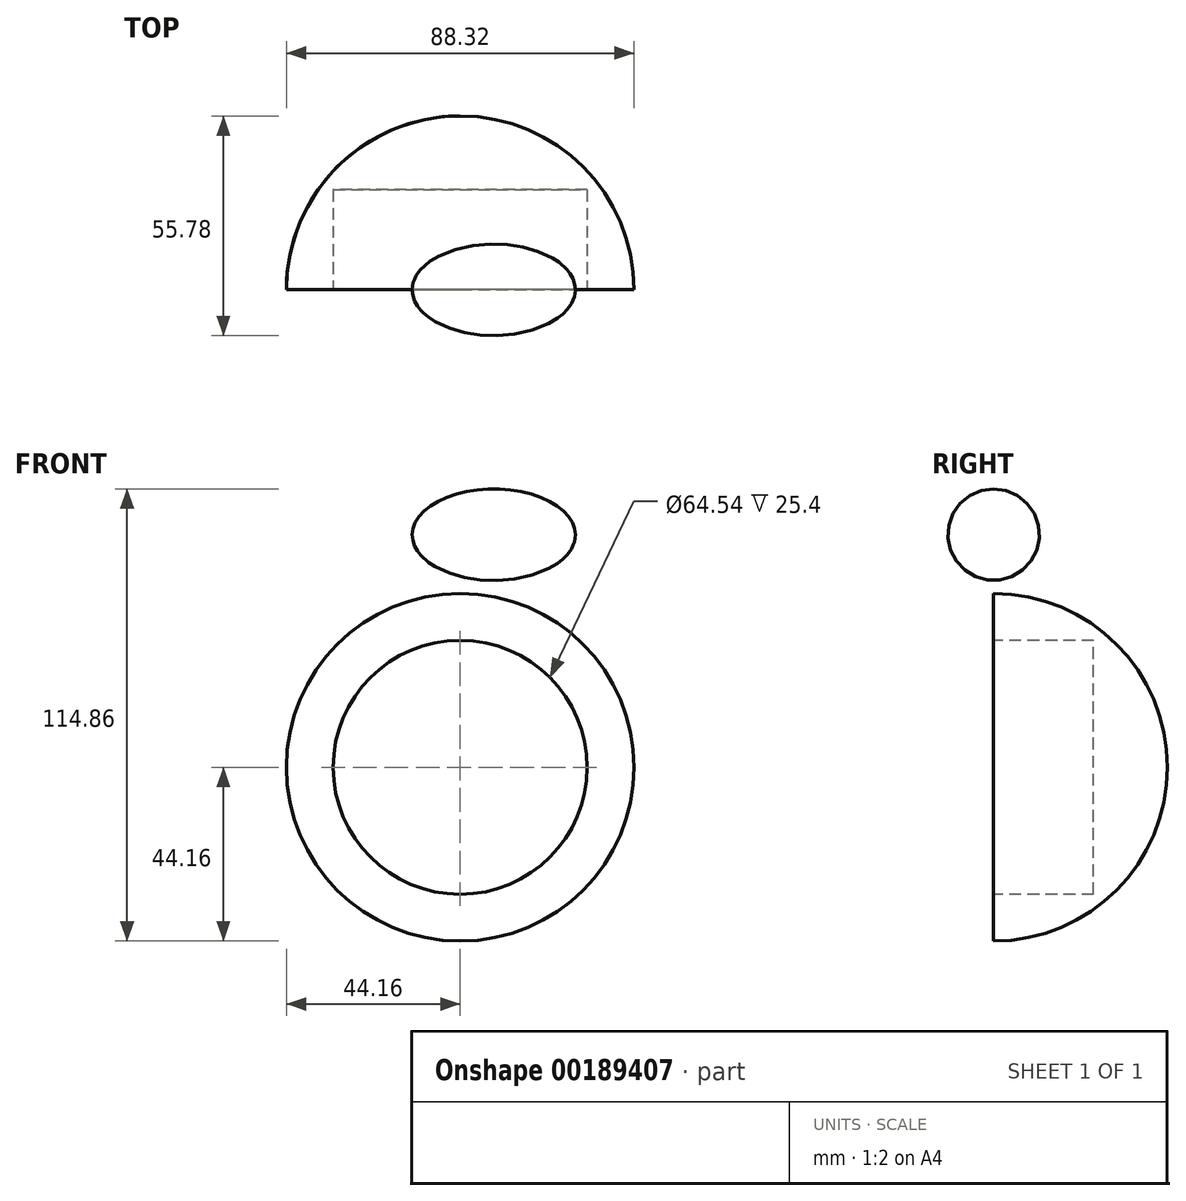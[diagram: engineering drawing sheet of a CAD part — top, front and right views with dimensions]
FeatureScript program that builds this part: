
annotation { "Feature Type Name" : "Feature", "Feature Type Description" : "" }
export const myFeature = defineFeature(function(context is Context, id is Id, definition is map)
    precondition{}
    {
        {
            var Q0;
            Q0=qCreatedBy(makeId("Top.planeOp"),FACE);
            var sketch = newSketch(context, id + "F0", { "sketchPlane" : qUnion([Q0])});
            skArc(sketch, "E0", {"start": v(44.16, 0) * mm, "mid": v(0, 44.16) * mm, "end": v(-44.16, 0) * mm});
            skLineSegment(sketch, "E1", {"start": v(44.16, 0) * mm, "end": v(-44.16, 0) * mm});
            skLineSegment(sketch, "E2", {"start": v(0, 0) * mm, "end": v(0, 44.16) * mm});
            skSolve(sketch);
        }
        {
            var Q0;
            {var subQ3=sQuery(id+"F0.wireOp",EDGE,"E2");Q0=makeQuery(id+"F0.imprint","IMPRINT",FACE,{"disambiguationData":[TD([[makeQuery(id+"F0.imprint","IMPRINT",EDGE,{"derivedFrom":subQ3}),1.0]])]});}
            var Q1;
            Q1=sQuery(id+"F0.wireOp",EDGE,"E2");
            revolve(context, id + "F1", {"entities" : qUnion([Q0]), "axis" : qUnion([Q1]), "revolveType" : RevolveType.FULL});
        }
        {
            var Q0;
            Q0=makeQuery(id+"F1.opRevolve","SWEPT_FACE",FACE,{"disambiguationData":[OSD([sQuery(id+"F0.wireOp",EDGE,"E1")])]});
            var sketch = newSketch(context, id + "F2", { "sketchPlane" : qUnion([Q0])});
            skCircle(sketch, "E3", {"center": v(0, 0) * mm, "radius": 32.27 * mm});
            skSolve(sketch);
        }
        {
            var Q0;
            Q0=makeQuery(id+"F2.imprint","IMPRINT",FACE,{"disambiguationData":[TD([[makeQuery(id+"F2.imprint","IMPRINT",EDGE,{"derivedFrom":sQuery(id+"F2.wireOp",EDGE,"E3")}),1.0]])]});
            extrude(context, id + "F3", {"entities" : qUnion([Q0]), "operationType" : NewBodyOperationType.REMOVE, "oppositeDirection" : true, "depth" : 25.4 * mm});
        }
        {
            var Q0;
            Q0=qCreatedBy(makeId("Front.planeOp"),FACE);
            var sketch = newSketch(context, id + "F4", { "sketchPlane" : qUnion([Q0])});
            skLineSegment(sketch, "E4.bottom", {"start": v(-65.98, 62.48) * mm, "end": v(-12.3, 62.48) * mm});
            skLineSegment(sketch, "E4.top", {"start": v(-65.98, 55.92) * mm, "end": v(-12.3, 55.92) * mm});
            skLineSegment(sketch, "E4.left", {"start": v(-65.98, 62.48) * mm, "end": v(-65.98, 55.92) * mm});
            skEllipse(sketch, "E5", {"center": v(8.53, 59.08) * mm, "majorRadius": 20.7 * mm, "minorRadius": 11.62 * mm, "majorAxis": v(-1, 0)});
            skLineSegment(sketch, "E6", {"start": v(-12.18, 59.08) * mm, "end": v(29.24, 59.08) * mm});
            skSolve(sketch);
        }
        {
            var Q0;
            {var subQ0=sQuery(id+"F4.wireOp",EDGE,"E6");Q0=makeQuery(id+"F4.imprint","IMPRINT",FACE,{"disambiguationData":[TD([[makeQuery(id+"F4.imprint","IMPRINT",EDGE,{"derivedFrom":subQ0}),1.0]])]});}
            var Q1;
            Q1=sQuery(id+"F4.wireOp",EDGE,"E6");
            revolve(context, id + "F5", {"entities" : qUnion([Q0]), "axis" : qUnion([Q1]), "revolveType" : RevolveType.FULL});
        }
    });
